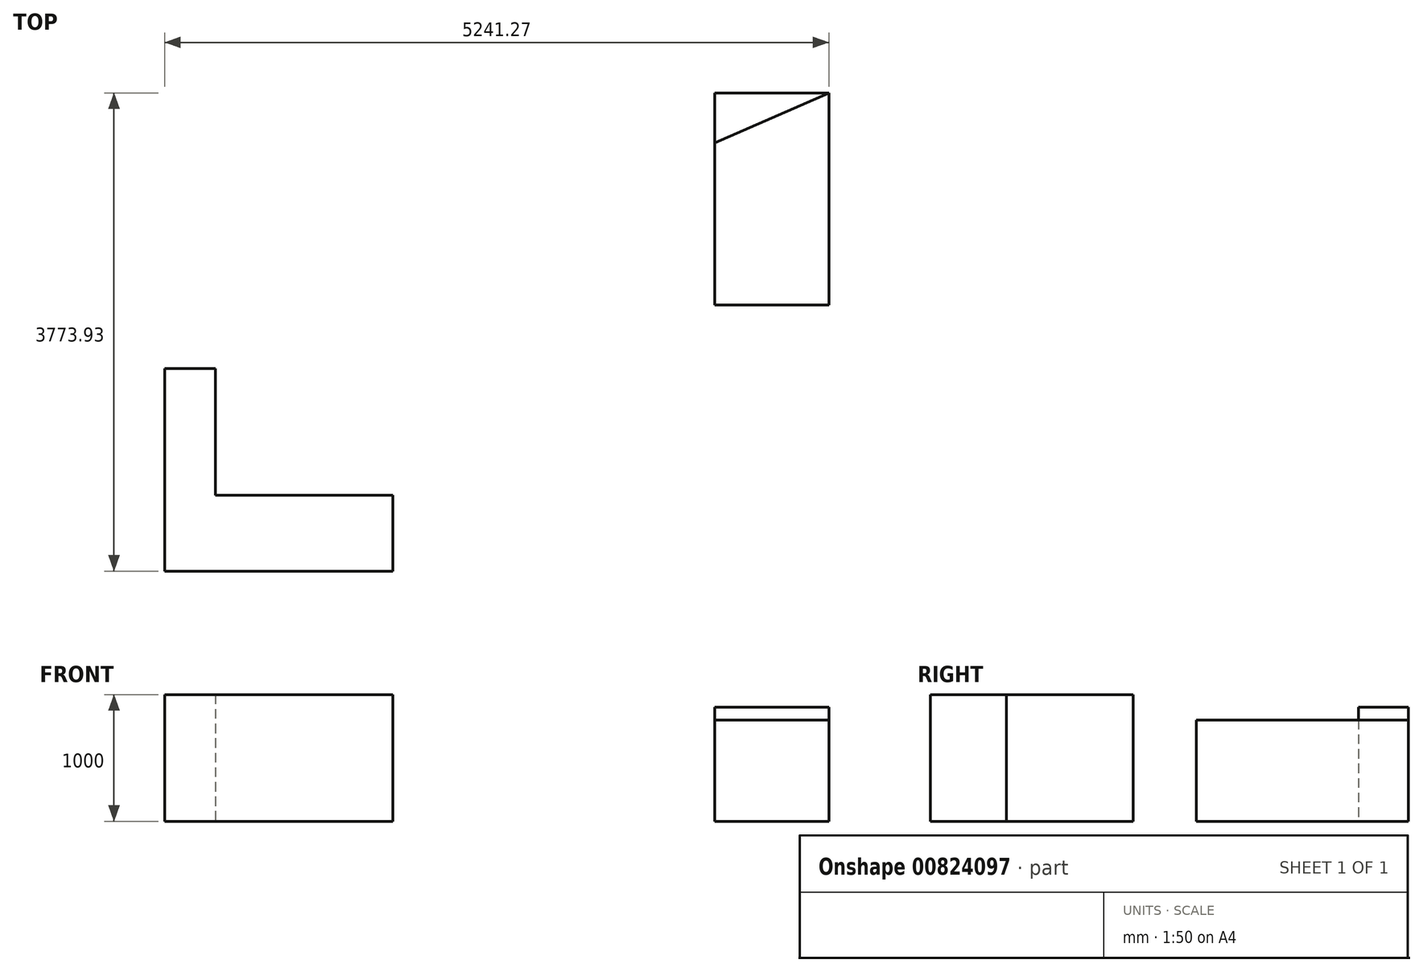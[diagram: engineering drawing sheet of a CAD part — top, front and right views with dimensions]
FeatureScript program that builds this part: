
annotation { "Feature Type Name" : "Feature", "Feature Type Description" : "" }
export const myFeature = defineFeature(function(context is Context, id is Id, definition is map)
    precondition{}
    {
        {
            var Q0;
            Q0=qCreatedBy(makeId("Top.planeOp"),FACE);
            var sketch = newSketch(context, id + "F0", { "sketchPlane" : qUnion([Q0])});
            skLineSegment(sketch, "E0.bottom", {"start": v(3000, 2000) * mm, "end": v(-3000, 2000) * mm});
            skLineSegment(sketch, "E0.top", {"start": v(3000, -2000) * mm, "end": v(-3000, -2000) * mm});
            skLineSegment(sketch, "E0.left", {"start": v(3000, 2000) * mm, "end": v(3000, -2000) * mm});
            skLineSegment(sketch, "E0.right", {"start": v(-3000, 2000) * mm, "end": v(-3000, -2000) * mm});
            skPoint(sketch, "E0.middle", {"position": v(0, 0) * mm});
            skLineSegment(sketch, "E1", {"start": v(-3000, -2000) * mm, "end": v(-3000, -400) * mm});
            skLineSegment(sketch, "E2", {"start": v(-3000, -2000) * mm, "end": v(-1200, -2000) * mm});
            skLineSegment(sketch, "E3", {"start": v(-1200, -2000) * mm, "end": v(-1200, -1400) * mm});
            skLineSegment(sketch, "E4", {"start": v(-3000, -400) * mm, "end": v(-2600, -400) * mm});
            skLineSegment(sketch, "E5", {"start": v(-2600, -400) * mm, "end": v(-2600, -1400) * mm});
            skLineSegment(sketch, "E6", {"start": v(-1200, -1400) * mm, "end": v(-2600, -1400) * mm});
            skLineSegment(sketch, "E7", {"start": v(1341.27, 2000) * mm, "end": v(2241.27, 2000) * mm});
            skLineSegment(sketch, "E8", {"start": v(2241.27, 2000) * mm, "end": v(2241.27, 100) * mm});
            skLineSegment(sketch, "E9", {"start": v(2241.27, 100) * mm, "end": v(1341.27, 100) * mm});
            skLineSegment(sketch, "E10", {"start": v(1341.27, 100) * mm, "end": v(1341.27, 2000) * mm});
            skLineSegment(sketch, "E11", {"start": v(1341.27, 1773.93) * mm, "end": v(2241.27, 1773.93) * mm});
            skLineSegment(sketch, "E12", {"start": v(2241.27, 1773.93) * mm, "end": v(1341.27, 1378.53) * mm});
            skSolve(sketch);
        }
        {
            var Q0;
            Q0=makeQuery(id+"F0.imprint","IMPRINT",FACE,{"disambiguationData":[TD([[makeQuery(id+"F0.imprint","IMPRINT",EDGE,{"derivedFrom":sQuery(id+"F0.wireOp",EDGE,"E1")}),-1.0]])]});
            var Q1;
            {var subQ0=sQuery(id+"F0.wireOp",EDGE,"E7");Q1=makeQuery(id+"F0.imprint","IMPRINT",FACE,{"disambiguationData":[TD([[makeQuery(id+"F0.imprint","IMPRINT",EDGE,{"derivedFrom":subQ0}),-1.0]])]});}
            extrude(context, id + "F1", {"entities" : qUnion([Q0, Q1]), "depth" : 1000 * mm, "offsetDistance" : 25 * mm});
        }
        {
            var Q0;
            {var subQ0=sQuery(id+"F0.wireOp",EDGE,"E9");Q0=makeQuery(id+"F0.imprint","IMPRINT",FACE,{"disambiguationData":[TD([[makeQuery(id+"F0.imprint","IMPRINT",EDGE,{"derivedFrom":subQ0}),-1.0]])]});}
            extrude(context, id + "F2", {"entities" : qUnion([Q0]), "depth" : 800 * mm, "offsetDistance" : 25 * mm});
        }
        {
            var Q0;
            {var subQ0=sQuery(id+"F0.wireOp",EDGE,"E11");Q0=makeQuery(id+"F0.imprint","IMPRINT",FACE,{"disambiguationData":[TD([[makeQuery(id+"F0.imprint","IMPRINT",EDGE,{"derivedFrom":subQ0}),-1.0]])]});}
            extrude(context, id + "F3", {"entities" : qUnion([Q0]), "depth" : 900 * mm, "offsetDistance" : 25 * mm});
        }
    });
